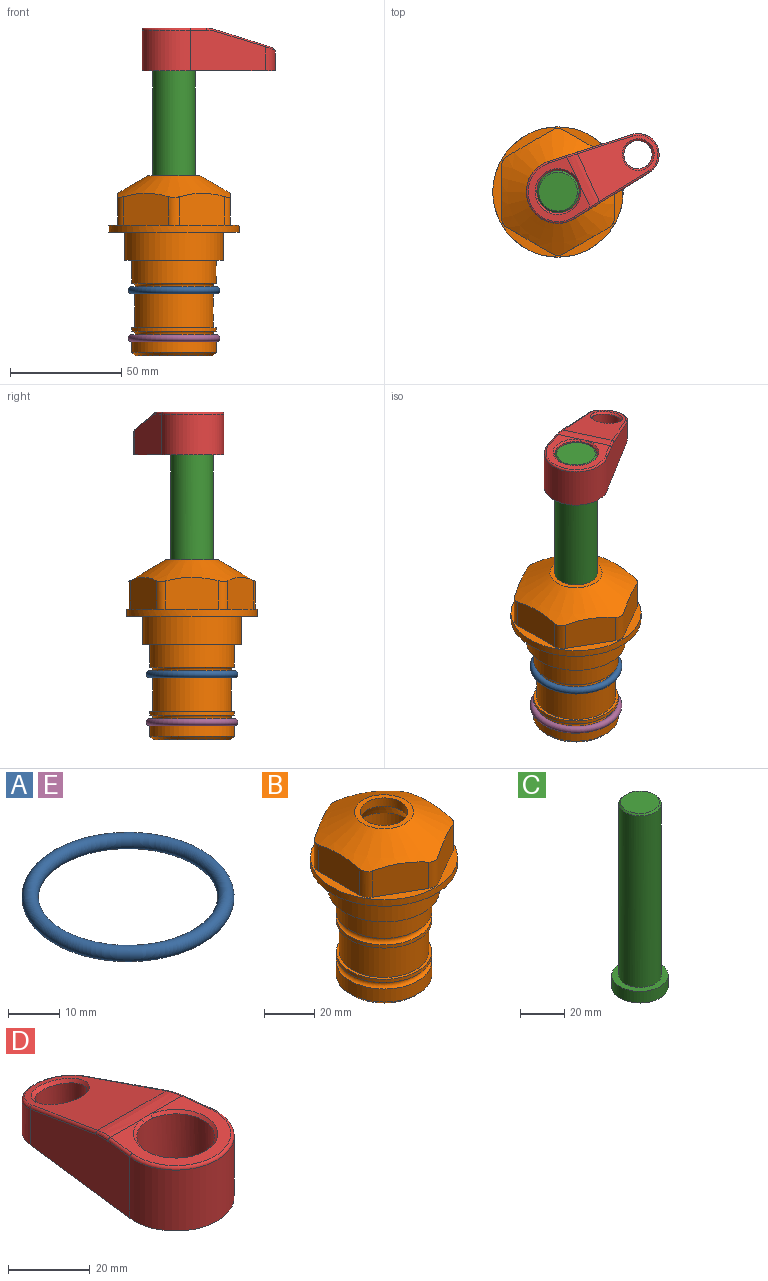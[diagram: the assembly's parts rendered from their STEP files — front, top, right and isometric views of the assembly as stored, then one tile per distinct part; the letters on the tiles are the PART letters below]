
ASSEMBLY  parts=5 mates=4
PART A: 1 faces, bbox 44.7x44.7x3.2 mm
  f0: torus R=19.05mm, axis (0,0,1), area 1193.9mm2
PART B: 36 faces, bbox 58.7x58.7x81 mm
  f0: cylinder r=17.78mm len=35.56mm, axis (0,0,1), area 1670.8mm2, adj f23,f24,f31
  f1: cylinder r=19.05mm len=38.1mm, axis (0,0,1), area 1191.9mm2, adj f26,f27,f30
  f2: plane 58.66x58.66mm, normal (0,0,-1), area 1150.6mm2, adj f3,f28
  f3: cylinder r=29.33mm len=58.66mm, axis (0,0,-1), area 585.1mm2, adj f2,f4
  f4: plane 58.66x58.66mm, normal (0,0,1), area 475.9mm2, adj f3,f5,f6,f7,f8,f9,f10,f11
  f5: plane 20.32x14.34mm, normal (-0.5,0.87,0), area 324.4mm2, adj f4,f15,f16,f17
  f6: plane 20.32x14.34mm, normal (0.5,0.87,0), area 324.4mm2, adj f4,f14,f15,f17
  f7: plane 23.48x14.34mm, normal (1,0,0), area 324.4mm2, adj f4,f13,f14,f17
  f8: plane 20.32x14.34mm, normal (0.5,-0.87,0), area 324.4mm2, adj f4,f12,f13,f17
  f9: plane 20.32x14.34mm, normal (-0.5,-0.87,0), area 324.4mm2, adj f4,f11,f12,f17
  f10: plane 23.48x14.34mm, normal (-1,0,0), area 324.4mm2, adj f4,f11,f16,f17
  f11: cylinder r=5.08mm len=12.85mm, axis (0,0,-1), area 67.2mm2, adj f4,f9,f10,f17
  f12: cylinder r=5.08mm len=12.85mm, axis (0,0,-1), area 67.2mm2, adj f4,f8,f9,f17
  f13: cylinder r=5.08mm len=12.85mm, axis (0,0,-1), area 67.2mm2, adj f4,f7,f8,f17
  f14: cylinder r=5.08mm len=12.85mm, axis (0,0,-1), area 67.2mm2, adj f4,f6,f7,f17
  f15: cylinder r=5.08mm len=12.85mm, axis (0,0,-1), area 67.2mm2, adj f4,f5,f6,f17
  f16: cylinder r=5.08mm len=12.85mm, axis (0,0,-1), area 67.2mm2, adj f4,f5,f10,f17
  f17: cone r=11.73mm half-angle=60deg, axis (0,0,-1), area 2071.8mm2, adj f5,f6,f7,f8,f9,f10,f11,f12
  f18: plane 23.46x23.46mm, normal (0,0,1), area 147.4mm2, adj f17,f35
  f19: plane 34.93x34.93mm, normal (0,0,-1), area 958mm2, adj f29
  f20: cylinder r=19.05mm len=38.1mm, axis (0,0,1), area 760.1mm2, adj f21,f29
  f21: torus R=19.05mm, axis (0,0,1), area 565.3mm2, adj f20,f22
  f22: cylinder r=19.05mm len=38.1mm, axis (0,0,1), area 190mm2, adj f21,f23
  f23: plane 38.1x38.1mm, normal (0,0,1), area 146.9mm2, adj f0,f22
  f24: plane 38.1x38.1mm, normal (0,0,-1), area 146.9mm2, adj f0,f25
  f25: cylinder r=19.05mm len=38.1mm, axis (0,0,1), area 190mm2, adj f24,f26
  f26: torus R=19.05mm, axis (0,0,1), area 565.3mm2, adj f1,f25
  f27: plane 44.45x44.45mm, normal (0,0,-1), area 411.7mm2, adj f1,f28
  f28: cylinder r=22.23mm len=44.45mm, axis (0,0,1), area 1773.5mm2, adj f2,f27
  f29: cone r=19.05mm half-angle=45deg, axis (0,0,1), area 257.5mm2, adj f19,f20
  f30: cylinder r=3.17mm len=6.75mm, axis (-1,0,0), area 128mm2, adj f1,f33
  f31: cylinder r=3.17mm len=6.35mm, axis (-1,0,0), area 102.5mm2, adj f0,f33
  f32: plane 25.4x25.4mm, normal (0,0,1), area 506.7mm2, adj f33
  f33: cylinder r=12.7mm len=66.42mm, axis (0,0,-1), area 5236.2mm2, adj f30,f31,f32,f34
  f34: cone r=9.53mm half-angle=30deg, axis (0,0,-1), area 443.4mm2, adj f33,f35
  f35: cylinder r=9.53mm len=19.05mm, axis (0,0,-1), area 240.9mm2, adj f18,f34
PART C: 6 faces, bbox 25.4x25.4x101.6 mm
  f0: plane 17.46x17.46mm, normal (0,0,1), area 239.5mm2, adj f5
  f1: plane 25.4x25.4mm, normal (0,0,-1), area 506.7mm2, adj f2
  f2: cylinder r=12.7mm len=25.4mm, axis (0,0,1), area 506.7mm2, adj f1,f3
  f3: plane 25.4x25.4mm, normal (0,0,1), area 221.7mm2, adj f2,f4
  f4: cylinder r=9.53mm len=94.46mm, axis (0,0,1), area 5653mm2, adj f3,f5
  f5: cone r=8.73mm half-angle=45deg, axis (0,0,-1), area 64.4mm2, adj f0,f4
PART D: 31 faces, bbox 31.7x65.5x19.8 mm
  f0: plane 39.12x18.26mm, normal (0.99,0.12,0), area 612.2mm2, adj f1,f4,f7,f11,f13,f15
  f1: cylinder r=9.53mm len=18.91mm, axis (0,0,-1), area 296.1mm2, adj f0,f2,f7,f17
  f2: plane 39.12x18.26mm, normal (-0.99,0.12,0), area 612.2mm2, adj f1,f4,f7,f12,f14,f16
  f3: cylinder r=6.35mm len=12.7mm, axis (0,0,-1), area 362.4mm2, adj f7,f18
  f4: cylinder r=14.29mm len=28.58mm, axis (0,0,-1), area 882.2mm2, adj f0,f2,f7,f10
  f5: cylinder r=9.53mm len=19.05mm, axis (0,0,-1), area 1092.6mm2, adj f7,f19,f20
  f6: plane 26.99x23.69mm, normal (0,0,1), area 216.2mm2, adj f9,f10,f11,f12,f19
  f7: plane 63.5x28.58mm, normal (0,0,-1), area 661.8mm2, adj f0,f1,f2,f3,f4,f5,f22,f23
  f8: plane 33.52x23.6mm, normal (0,0.26,0.97), area 486mm2, adj f9,f15,f16,f17,f18
  f9: cylinder r=19.05mm len=24.72mm, axis (1,0,0), area 120.4mm2, adj f6,f8,f13,f14,f20
  f10: torus R=13.49mm, axis (0,0,1), area 59mm2, adj f4,f6,f11,f12
  f11: cylinder r=0.79mm len=8.67mm, axis (0.12,-0.99,0), area 10.8mm2, adj f0,f6,f10,f13
  f12: cylinder r=0.79mm len=8.67mm, axis (0.12,0.99,0), area 10.8mm2, adj f2,f6,f10,f14
  f13: bspline ~4.95x1.42mm, area 6.1mm2, adj f0,f9,f11,f15
  f14: bspline ~4.95x1.42mm, area 6.1mm2, adj f2,f9,f12,f16
  f15: cylinder r=0.79mm len=25.95mm, axis (0.12,-0.96,0.26), area 32.9mm2, adj f0,f8,f13,f17
  f16: cylinder r=0.79mm len=25.95mm, axis (0.12,0.96,-0.26), area 32.9mm2, adj f2,f8,f14,f17
  f17: bspline ~18.91x8.38mm, area 30mm2, adj f1,f8,f15,f16
  f18: bspline ~14.29x14.29mm, area 48.3mm2, adj f3,f8
  f19: cone r=9.53mm half-angle=45deg, axis (0,0,1), area 66.5mm2, adj f5,f6,f20
  f20: bspline ~3.22x0.96mm, area 3.5mm2, adj f5,f9,f19
  f21: plane 2.75x2.72mm, normal (0,0,-1), area 2.9mm2, adj f23,f25,f28
  f22: plane 23.05x15.88mm, normal (-0.99,-0.12,0), area 323.6mm2, adj f7,f25,f26,f27,f28,f29
  f23: plane 23.05x15.88mm, normal (0.99,-0.12,0), area 323.6mm2, adj f7,f21,f25,f27,f28,f30
  f24: cylinder r=9.53mm len=10.69mm, axis (0,0,-1), area 114.7mm2, adj f7,f27,f29,f30
  f25: cylinder r=12.7mm len=20.59mm, axis (0,0,-1), area 381.1mm2, adj f7,f21,f22,f23,f26,f28
  f26: plane 2.75x2.72mm, normal (0,0,-1), area 2.9mm2, adj f22,f25,f28
  f27: plane 19.72x18.37mm, normal (0,-0.26,-0.97), area 291.8mm2, adj f22,f23,f24,f28,f29,f30
  f28: cylinder r=15.88mm len=19.92mm, axis (1,0,0), area 54.8mm2, adj f21,f22,f23,f25,f26,f27
  f29: cylinder r=1.59mm len=11mm, axis (0,0,-1), area 34.7mm2, adj f7,f22,f24,f27
  f30: cylinder r=1.59mm len=11mm, axis (0,0,-1), area 34.7mm2, adj f7,f23,f24,f27
PART E: same geometry as A
PLACE A t=(0,0,-1.59)mm
PLACE B at identity fixed
PLACE C rot(axis=(0,0,-1),65.2deg) t=(0,0,27.55)mm
PLACE D rot(axis=(0,0,-1),65.2deg) t=(0,0,28.35)mm
PLACE E t=(0,0,-23.18)mm
MATE fastened E.f0 <-> B.f0  axis (0,0,1) through (0,0,-47.69)mm
MATE fastened D.f4 <-> C.f2  axis (0,0,-1) through (0,0,91.05)mm
MATE cylindrical B.f0 <-> C.f2  axis (0,0,1) through (0,0,-50.55)mm
MATE fastened A.f0 <-> B.f0  axis (0,0,1) through (0,0,-26.1)mm
